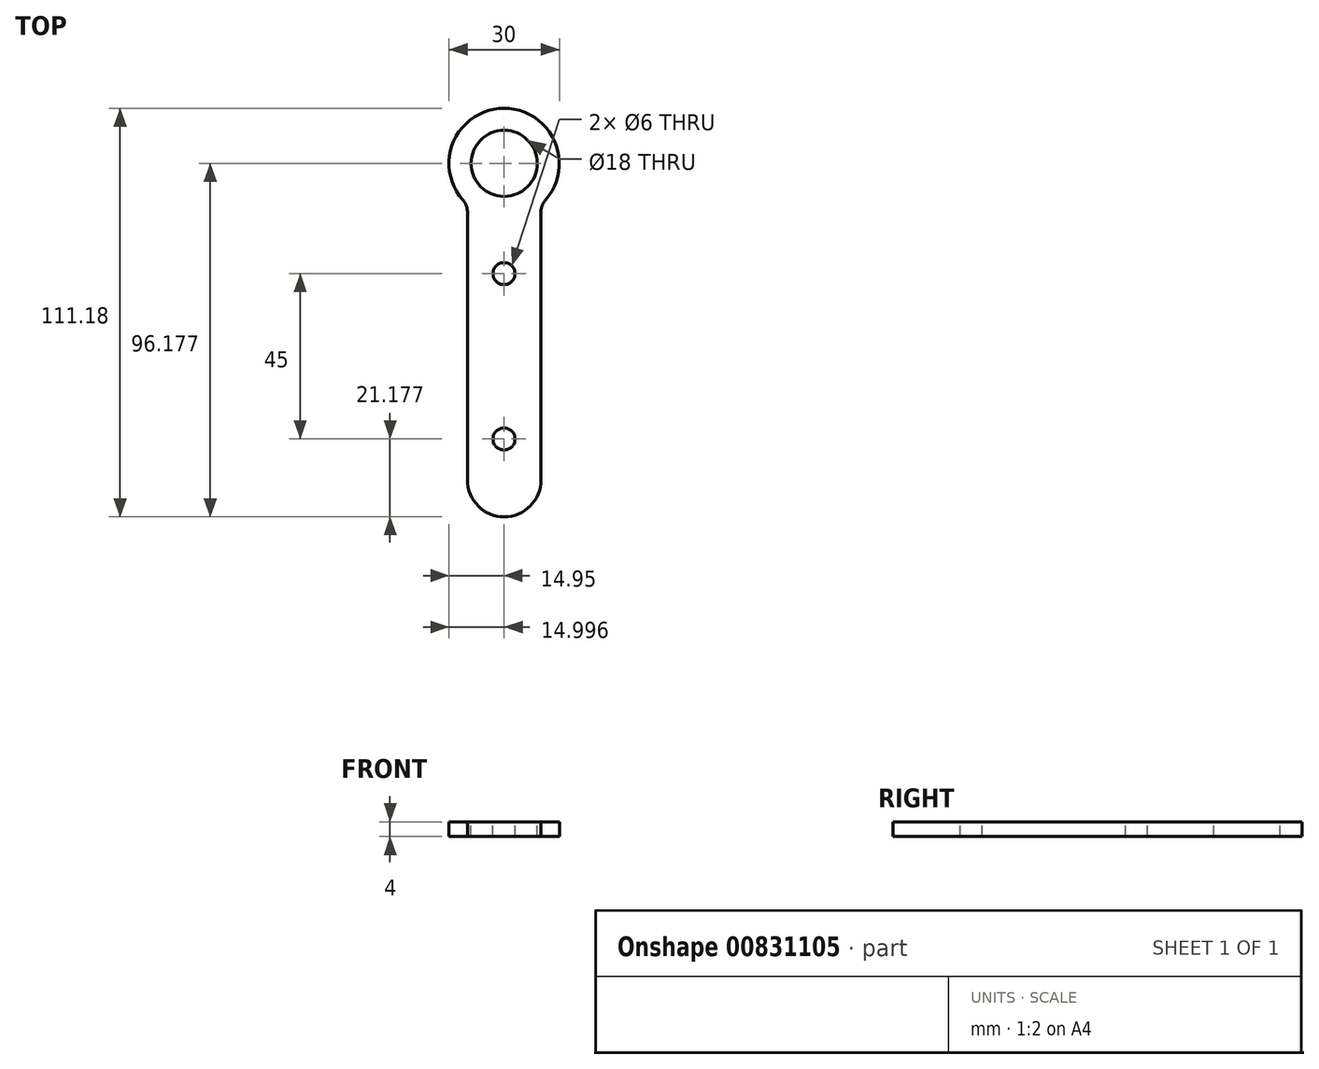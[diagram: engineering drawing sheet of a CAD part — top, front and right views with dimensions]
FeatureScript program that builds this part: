
annotation { "Feature Type Name" : "Feature", "Feature Type Description" : "" }
export const myFeature = defineFeature(function(context is Context, id is Id, definition is map)
    precondition{}
    {
        {
            var Q0;
            Q0=qCreatedBy(makeId("Top.planeOp"),FACE);
            var sketch = newSketch(context, id + "F0", { "sketchPlane" : qUnion([Q0])});
            skLineSegment(sketch, "E0", {"start": v(-9.95, 11.02) * mm, "end": v(-9.95, -61.93) * mm});
            skLineSegment(sketch, "E1", {"start": v(10.05, -61.93) * mm, "end": v(10.05, 11.02) * mm});
            skArc(sketch, "E2", {"start": v(-9.95, -61.93) * mm, "mid": v(0.05, -71.93) * mm, "end": v(10.05, -61.93) * mm});
            skArc(sketch, "E3", {"start": v(11.3, 14.33) * mm, "mid": v(0.05, 39.25) * mm, "end": v(-11.2, 14.33) * mm});
            skPoint(sketch, "E4.visualSharp", {"position": v(-9.95, 13.07) * mm});
            skArc(sketch, "E4.filletArc", {"start": v(-9.95, 11.02) * mm, "mid": v(-10.28, 12.79) * mm, "end": v(-11.2, 14.33) * mm});
            skPoint(sketch, "E5.visualSharp", {"position": v(10.05, 13.07) * mm});
            skArc(sketch, "E5.filletArc", {"start": v(11.3, 14.33) * mm, "mid": v(10.37, 12.79) * mm, "end": v(10.05, 11.02) * mm});
            skSolve(sketch);
        }
        {
            var Q0;
            Q0 = qSketchRegion(id + "F0", true);
            extrude(context, id + "F1", {"entities" : qUnion([Q0]), "depth" : 4 * mm, "offsetDistance" : 25 * mm});
        }
        {
            var Q0;
            Q0=makeQuery(id+"F1.opExtrude","CAP_FACE",FACE,{"disambiguationData":[OSD([sQuery(id+"F0.wireOp",EDGE,"E0"),sQuery(id+"F0.wireOp",EDGE,"E1"),sQuery(id+"F0.wireOp",EDGE,"E2"),sQuery(id+"F0.wireOp",EDGE,"E3")])],"isStart":false});
            var sketch = newSketch(context, id + "F2", { "sketchPlane" : qUnion([Q0])});
            skCircle(sketch, "E6", {"center": v(0.05, 24.25) * mm, "radius": 9 * mm});
            skCircle(sketch, "E7.0.1.0", {"center": v(0, -5.75) * mm, "radius": 3 * mm});
            skCircle(sketch, "E7.0.2.0", {"center": v(0, -50.75) * mm, "radius": 3 * mm});
            skSolve(sketch);
        }
        {
            var Q0;
            Q0 = qSketchRegion(id + "F2", true);
            extrude(context, id + "F3", {"entities" : qUnion([Q0]), "operationType" : NewBodyOperationType.REMOVE, "endBound" : BoundingType.THROUGH_ALL, "oppositeDirection" : true, "depth" : 25 * mm, "offsetDistance" : 25 * mm});
        }
    });
